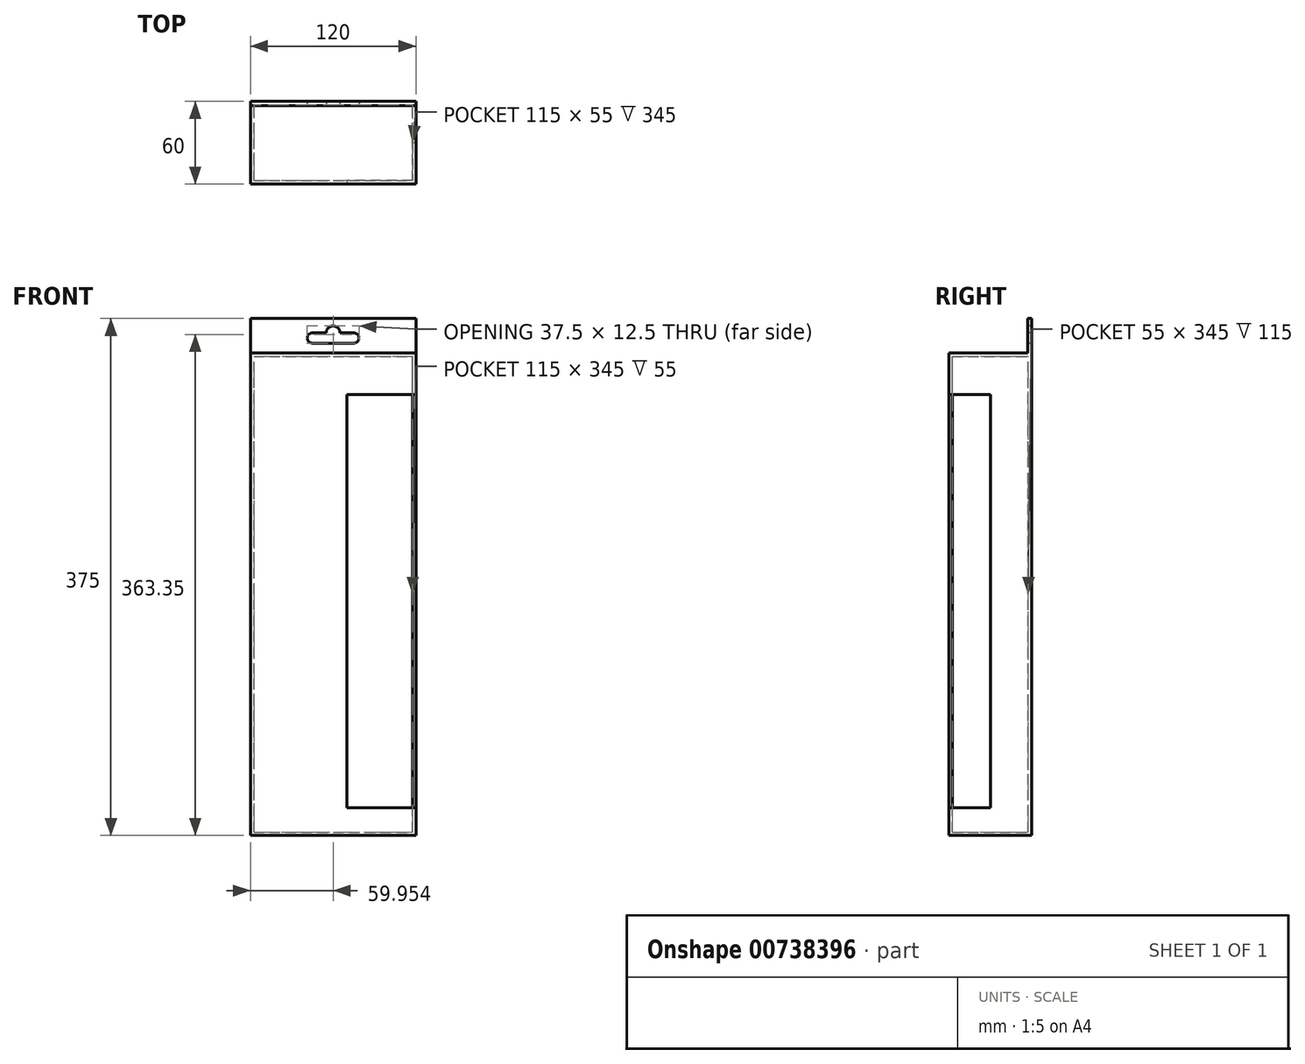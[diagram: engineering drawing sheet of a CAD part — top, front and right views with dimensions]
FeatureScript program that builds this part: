
annotation { "Feature Type Name" : "Feature", "Feature Type Description" : "" }
export const myFeature = defineFeature(function(context is Context, id is Id, definition is map)
    precondition{}
    {
        {
            var Q0;
            Q0=qCreatedBy(makeId("Front.planeOp"),FACE);
            var sketch = newSketch(context, id + "F0", { "sketchPlane" : qUnion([Q0])});
            skLineSegment(sketch, "E0.bottom", {"start": v(0, 0) * mm, "end": v(120, 0) * mm});
            skLineSegment(sketch, "E0.top", {"start": v(0, 350) * mm, "end": v(120, 350) * mm});
            skLineSegment(sketch, "E0.left", {"start": v(0, 0) * mm, "end": v(0, 350) * mm});
            skLineSegment(sketch, "E0.right", {"start": v(120, 0) * mm, "end": v(120, 350) * mm});
            skSolve(sketch);
        }
        {
            var Q0;
            Q0 = qSketchRegion(id + "F0", true);
            extrude(context, id + "F1", {"entities" : qUnion([Q0]), "depth" : 60 * mm, "offsetDistance" : 25 * mm});
        }
        {
            var Q0;
            Q0=makeQuery(id+"F1.opExtrude","CAP_FACE",FACE,{"disambiguationData":[OSD([sQuery(id+"F0.wireOp",EDGE,"E0.bottom"),sQuery(id+"F0.wireOp",EDGE,"E0.top"),sQuery(id+"F0.wireOp",EDGE,"E0.left"),sQuery(id+"F0.wireOp",EDGE,"E0.right")])],"isStart":false});
            var sketch = newSketch(context, id + "F2", { "sketchPlane" : qUnion([Q0])});
            skLineSegment(sketch, "E1", {"start": v(120, 0) * mm, "end": v(120, 20) * mm});
            skLineSegment(sketch, "E2.bottom", {"start": v(120, 20) * mm, "end": v(70, 20) * mm});
            skLineSegment(sketch, "E2.top", {"start": v(120, 320) * mm, "end": v(70, 320) * mm});
            skLineSegment(sketch, "E2.left", {"start": v(120, 20) * mm, "end": v(120, 320) * mm});
            skLineSegment(sketch, "E2.right", {"start": v(70, 20) * mm, "end": v(70, 320) * mm});
            skSolve(sketch);
        }
        {
            var Q0;
            Q0=makeQuery(id+"F2.imprint","IMPRINT",FACE,{"disambiguationData":[TD([[makeQuery(id+"F2.imprint","IMPRINT",EDGE,{"derivedFrom":sQuery(id+"F2.wireOp",EDGE,"E2.bottom")}),-1.0]])]});
            extrude(context, id + "F3", {"entities" : qUnion([Q0]), "operationType" : NewBodyOperationType.REMOVE, "oppositeDirection" : true, "depth" : 30 * mm, "offsetDistance" : 25 * mm});
        }
        {
            var Q0;
            Q0=makeQuery(id+"F3.boolean.opBoolean","COPY",FACE,{"derivedFrom":makeQuery(id+"F3.opExtrude","SWEPT_FACE",FACE,{"disambiguationData":[OSD([sQuery(id+"F2.wireOp",EDGE,"E2.bottom")])]})});
            var Q1;
            Q1=makeQuery(id+"F3.boolean.opBoolean","COPY",FACE,{"derivedFrom":makeQuery(id+"F3.opExtrude","SWEPT_FACE",FACE,{"disambiguationData":[OSD([sQuery(id+"F2.wireOp",EDGE,"E2.right")])]})});
            var Q2;
            Q2=makeQuery(id+"F3.boolean.opBoolean","COPY",FACE,{"derivedFrom":makeQuery(id+"F3.opExtrude","CAP_FACE",FACE,{"disambiguationData":[OSD([sQuery(id+"F2.wireOp",EDGE,"E2.bottom"),sQuery(id+"F2.wireOp",EDGE,"E2.top"),sQuery(id+"F2.wireOp",EDGE,"E2.left"),sQuery(id+"F2.wireOp",EDGE,"E2.right")])],"isStart":false})});
            var Q3;
            Q3=makeQuery(id+"F3.boolean.opBoolean","COPY",FACE,{"derivedFrom":makeQuery(id+"F3.opExtrude","SWEPT_FACE",FACE,{"disambiguationData":[OSD([sQuery(id+"F2.wireOp",EDGE,"E2.top")])]})});
            shell(context, id + "F4", {"entities" : qUnion([Q0, Q1, Q2, Q3]), "thickness" : 2.5 * mm});
        }
        {
            var Q0;
            Q0=makeQuery(id+"F1.opExtrude","SWEPT_FACE",FACE,{"disambiguationData":[OSD([sQuery(id+"F0.wireOp",EDGE,"E0.top")])]});
            var sketch = newSketch(context, id + "F5", { "sketchPlane" : qUnion([Q0])});
            skLineSegment(sketch, "E3.bottom", {"start": v(120, 0) * mm, "end": v(0, 0) * mm});
            skLineSegment(sketch, "E3.top", {"start": v(120, -3) * mm, "end": v(0, -3) * mm});
            skLineSegment(sketch, "E3.left", {"start": v(120, 0) * mm, "end": v(120, -3) * mm});
            skLineSegment(sketch, "E3.right", {"start": v(0, 0) * mm, "end": v(0, -3) * mm});
            skSolve(sketch);
        }
        {
            var Q0;
            Q0 = qSketchRegion(id + "F5", true);
            extrude(context, id + "F6", {"entities" : qUnion([Q0]), "operationType" : NewBodyOperationType.ADD, "depth" : 25 * mm, "offsetDistance" : 25 * mm});
        }
        {
            var Q0;
            Q0=makeQuery(id+"F6.opExtrude","SWEPT_FACE",FACE,{"disambiguationData":[OSD([sQuery(id+"F5.wireOp",EDGE,"E3.top")])]});
            var sketch = newSketch(context, id + "F7", { "sketchPlane" : qUnion([Q0])});
            skLineSegment(sketch, "E4", {"start": v(60, 375) * mm, "end": v(60, 365) * mm});
            skLineSegment(sketch, "E5.bottom", {"start": v(74.95, 364.6) * mm, "end": v(64.95, 364.6) * mm});
            skLineSegment(sketch, "E5.top", {"start": v(74.95, 357.1) * mm, "end": v(44.95, 357.1) * mm});
            skArc(sketch, "E6", {"start": v(44.95, 364.6) * mm, "mid": v(41.2, 360.85) * mm, "end": v(44.95, 357.1) * mm});
            skArc(sketch, "E7", {"start": v(74.95, 357.1) * mm, "mid": v(78.7, 360.85) * mm, "end": v(74.95, 364.6) * mm});
            skLineSegment(sketch, "E8.trimOffspring", {"start": v(54.95, 364.6) * mm, "end": v(44.95, 364.6) * mm});
            skArc(sketch, "E9", {"start": v(64.95, 364.6) * mm, "mid": v(59.95, 369.6) * mm, "end": v(54.95, 364.6) * mm});
            skSolve(sketch);
        }
        {
            var Q0;
            {var subQ0=sQuery(id+"F7.wireOp",EDGE,"E5.bottom");Q0=makeQuery(id+"F7.imprint","IMPRINT",FACE,{"disambiguationData":[TD([[makeQuery(id+"F7.imprint","IMPRINT",EDGE,{"derivedFrom":subQ0}),1.0]])]});}
            extrude(context, id + "F8", {"entities" : qUnion([Q0]), "operationType" : NewBodyOperationType.REMOVE, "oppositeDirection" : true, "depth" : 25 * mm, "offsetDistance" : 25 * mm});
        }
    });
